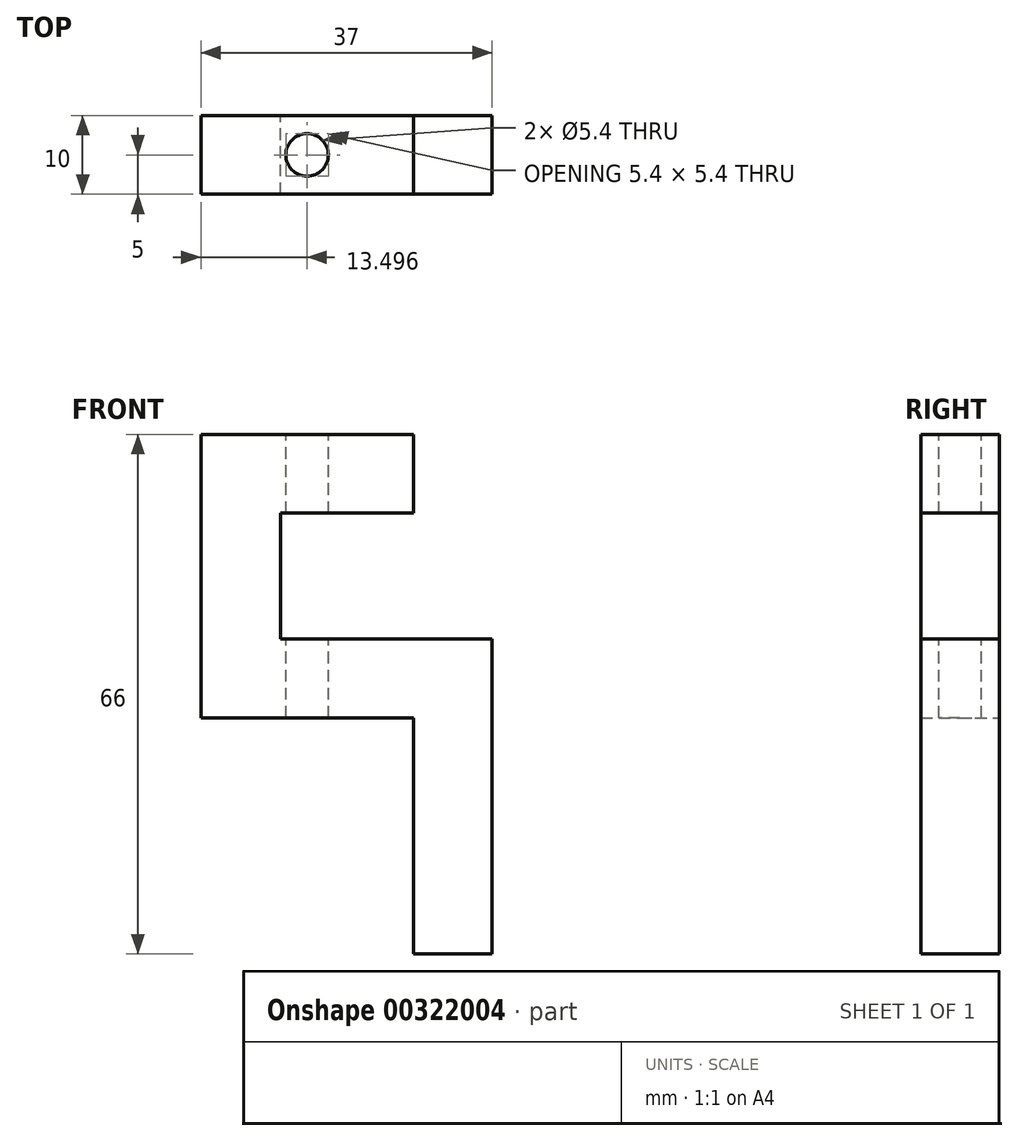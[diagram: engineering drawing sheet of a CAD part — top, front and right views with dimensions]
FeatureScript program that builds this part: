
annotation { "Feature Type Name" : "Feature", "Feature Type Description" : "" }
export const myFeature = defineFeature(function(context is Context, id is Id, definition is map)
    precondition{}
    {
        {
            assignVariable(context, id + "F0", {"name" : "Dvis", "anyValue" : 5.4 * mm});
        }
        {
            var Q0;
            Q0=qCreatedBy(makeId("Front.planeOp"),FACE);
            var sketch = newSketch(context, id + "F1", { "sketchPlane" : qUnion([Q0])});
            skLineSegment(sketch, "E0", {"start": v(-63.87, 13.78) * mm, "end": v(-36.87, 13.78) * mm});
            skLineSegment(sketch, "E1", {"start": v(-63.87, 13.78) * mm, "end": v(-63.87, -22.22) * mm});
            skLineSegment(sketch, "E2", {"start": v(-36.87, -12.22) * mm, "end": v(-53.77, -12.22) * mm});
            skLineSegment(sketch, "E3", {"start": v(-53.77, -12.22) * mm, "end": v(-53.77, 3.78) * mm});
            skLineSegment(sketch, "E4", {"start": v(-53.77, 3.78) * mm, "end": v(-36.87, 3.78) * mm});
            skLineSegment(sketch, "E5", {"start": v(-36.87, 3.78) * mm, "end": v(-36.87, 13.78) * mm});
            skLineSegment(sketch, "E6", {"start": v(-63.87, -22.22) * mm, "end": v(-36.87, -22.22) * mm});
            skLineSegment(sketch, "E7", {"start": v(-36.87, -12.22) * mm, "end": v(-26.87, -12.22) * mm});
            skLineSegment(sketch, "E8", {"start": v(-26.87, -12.22) * mm, "end": v(-26.87, -52.22) * mm});
            skLineSegment(sketch, "E9", {"start": v(-36.87, -22.22) * mm, "end": v(-36.87, -52.22) * mm});
            skLineSegment(sketch, "E10", {"start": v(-36.87, -52.22) * mm, "end": v(-26.87, -52.22) * mm});
            skSolve(sketch);
        }
        {
            var Q0;
            Q0=makeQuery(id+"F1.imprint","IMPRINT",FACE,{"disambiguationData":[TD([[makeQuery(id+"F1.imprint","IMPRINT",EDGE,{"derivedFrom":sQuery(id+"F1.wireOp",EDGE,"E0")}),-1.0]])]});
            var Q1;
            Q1 = qSketchRegion(id + "F3", true);
            extrude(context, id + "F2", {"entities" : qUnion([Q0, Q1]), "depth" : 10 * mm, "hasDraft" : true, "draftAngle" : 0 * degree});
        }
        {
            var Q0;
            Q0=makeQuery(id+"F2.opExtrude","SWEPT_FACE",FACE,{"disambiguationData":[OSD([sQuery(id+"F1.wireOp",EDGE,"E0")])]});
            var sketch = newSketch(context, id + "F3", { "sketchPlane" : qUnion([Q0])});
            skCircle(sketch, "E11", {"center": v(-50.37, -5) * mm, "radius": 2.7 * mm});
            skPoint(sketch, "E11.centerSnap0", {"position": v(-50.37, 0) * mm});
            skPoint(sketch, "E11.centerSnap1", {"position": v(-63.87, -5) * mm});
            skCircle(sketch, "E12", {"center": v(-56.82, -5) * mm, "radius": 2 * mm});
            skCircle(sketch, "E13", {"center": v(-43.92, -5) * mm, "radius": 2 * mm});
            skPoint(sketch, "E13.centerSnap0", {"position": v(-36.87, -5) * mm});
            skLineSegment(sketch, "E14", {"start": v(-56.82, -5) * mm, "end": v(-50.37, -5) * mm});
            skLineSegment(sketch, "E15", {"start": v(-50.37, -5) * mm, "end": v(-43.92, -5) * mm});
            skSolve(sketch);
        }
        {
            var Q0;
            Q0=sQuery(id+"F3.wireOp",VERTEX,"E11.center");
            var Q1;
            Q1=makeQuery(id+"F2.opExtrude","SWEPT_BODY",BODY,{"disambiguationData":[OSD([sQuery(id+"F1.wireOp",EDGE,"E0"),sQuery(id+"F1.wireOp",EDGE,"E1"),sQuery(id+"F1.wireOp",EDGE,"E2"),sQuery(id+"F1.wireOp",EDGE,"E3"),sQuery(id+"F1.wireOp",EDGE,"E4"),sQuery(id+"F1.wireOp",EDGE,"E5"),sQuery(id+"F1.wireOp",EDGE,"E6"),sQuery(id+"F1.wireOp",EDGE,"E7"),sQuery(id+"F1.wireOp",EDGE,"E8"),sQuery(id+"F1.wireOp",EDGE,"E9"),sQuery(id+"F1.wireOp",EDGE,"E10")])]});
            hole(context, id + "F4", {"style" : HoleStyle.SIMPLE, "endStyle" : HoleEndStyle.THROUGH, "holeDiameter" : getVariable(context, 'Dvis'), "isTappedThrough" : true, "tappedDepth" : 12.7 * mm, "tapClearance" : 3, "locations" : qUnion([Q0]), "scope" : qUnion([Q1])});
        }
    });
